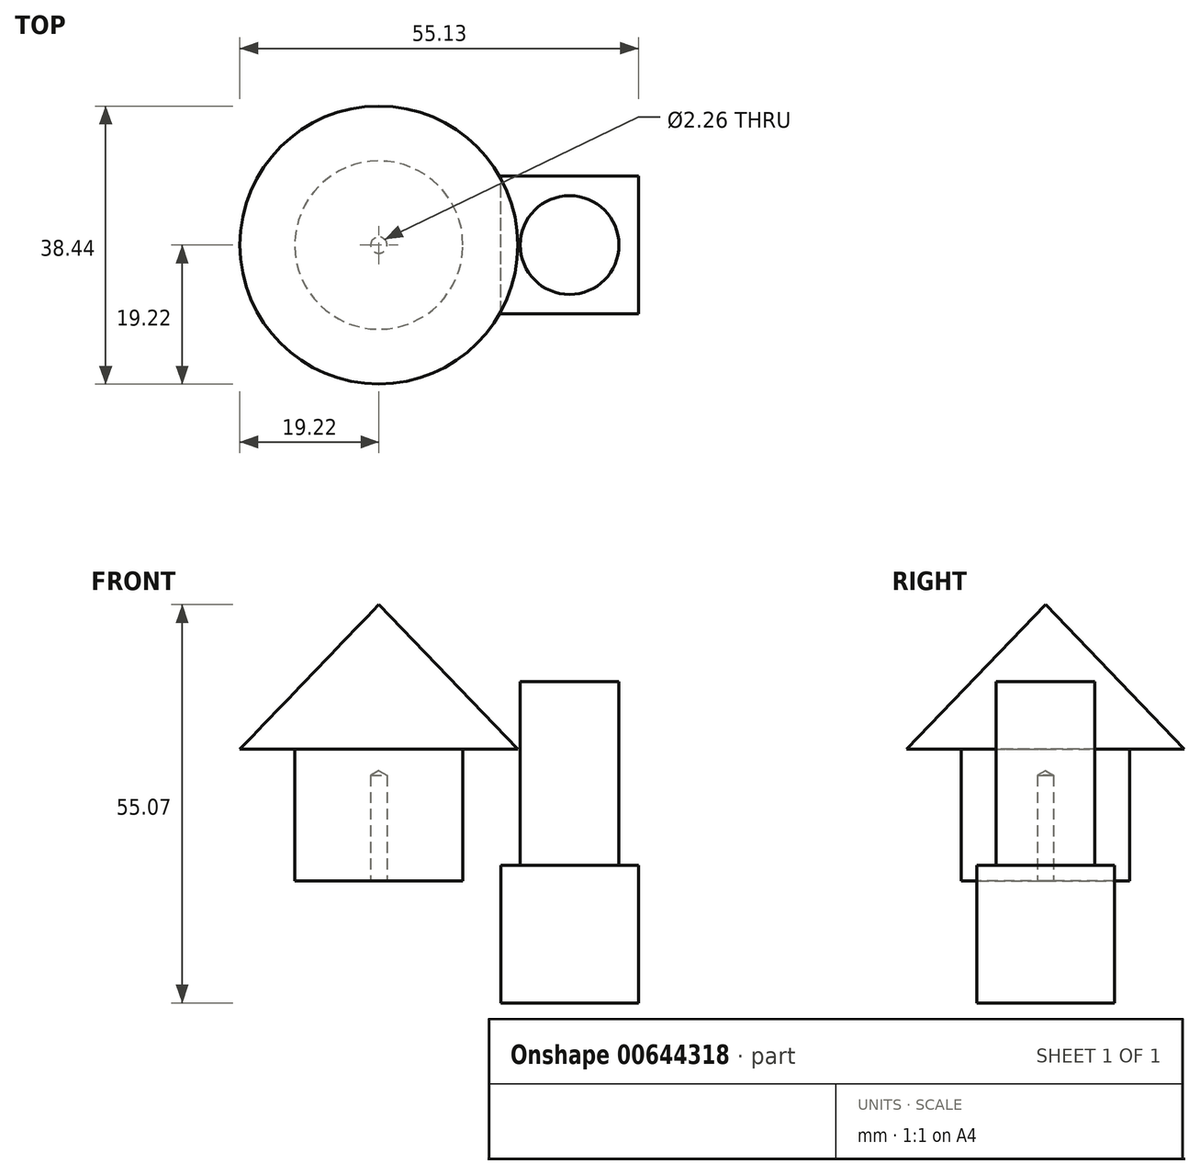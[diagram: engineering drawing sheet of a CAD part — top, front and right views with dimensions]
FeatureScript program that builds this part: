
annotation { "Feature Type Name" : "Feature", "Feature Type Description" : "" }
export const myFeature = defineFeature(function(context is Context, id is Id, definition is map)
    precondition{}
    {
        {
            var Q0;
            Q0=qCreatedBy(makeId("Top.planeOp"),FACE);
            var sketch = newSketch(context, id + "F0", { "sketchPlane" : qUnion([Q0])});
            skLineSegment(sketch, "E0.bottom", {"start": v(-9.53, -9.53) * mm, "end": v(9.53, -9.53) * mm});
            skLineSegment(sketch, "E0.top", {"start": v(-9.53, 9.53) * mm, "end": v(9.52, 9.53) * mm});
            skLineSegment(sketch, "E0.left", {"start": v(-9.53, -9.52) * mm, "end": v(-9.53, 9.53) * mm});
            skLineSegment(sketch, "E0.right", {"start": v(9.52, -9.52) * mm, "end": v(9.52, 9.53) * mm});
            skPoint(sketch, "E0.middle", {"position": v(0, 0) * mm});
            skSolve(sketch);
        }
        {
            var Q0;
            Q0 = qSketchRegion(id + "F0", true);
            extrude(context, id + "F1", {"entities" : qUnion([Q0]), "endBound" : BoundingType.SYMMETRIC, "depth" : 19.05 * mm, "offsetDistance" : 25.4 * mm});
        }
        {
            var Q0;
            Q0=makeQuery(id+"F1.opExtrude","CAP_FACE",FACE,{"disambiguationData":[OSD([sQuery(id+"F0.wireOp",EDGE,"E0.bottom"),sQuery(id+"F0.wireOp",EDGE,"E0.top"),sQuery(id+"F0.wireOp",EDGE,"E0.left"),sQuery(id+"F0.wireOp",EDGE,"E0.right")])],"isStart":false});
            var sketch = newSketch(context, id + "F2", { "sketchPlane" : qUnion([Q0])});
            skCircle(sketch, "E1", {"center": v(0, 0) * mm, "radius": 6.83 * mm});
            skSolve(sketch);
        }
        {
            var Q0;
            Q0 = qSketchRegion(id + "F2", true);
            extrude(context, id + "F3", {"entities" : qUnion([Q0]), "operationType" : NewBodyOperationType.ADD, "depth" : 25.4 * mm, "offsetDistance" : 25.4 * mm});
        }
        {
            var Q0;
            Q0=qCreatedBy(makeId("Front.planeOp"),FACE);
            var sketch = newSketch(context, id + "F4", { "sketchPlane" : qUnion([Q0])});
            skLineSegment(sketch, "E2", {"start": v(-26.38, 45.54) * mm, "end": v(-45.6, 25.56) * mm});
            skLineSegment(sketch, "E3", {"start": v(-45.6, 25.56) * mm, "end": v(-38.02, 25.56) * mm});
            skLineSegment(sketch, "E4", {"start": v(-38.02, 25.56) * mm, "end": v(-38.02, 7.32) * mm});
            skLineSegment(sketch, "E5", {"start": v(-38.02, 7.32) * mm, "end": v(-26.38, 7.32) * mm});
            skLineSegment(sketch, "E6", {"start": v(-26.38, 7.32) * mm, "end": v(-26.38, 45.54) * mm});
            skSolve(sketch);
        }
        {
            var Q0;
            Q0 = qSketchRegion(id + "F4", true);
            var Q1;
            Q1=sQuery(id+"F4.wireOp",EDGE,"E6");
            revolve(context, id + "F5", {"entities" : qUnion([Q0]), "axis" : qUnion([Q1]), "revolveType" : RevolveType.FULL});
        }
        {
            var Q0;
            Q0=makeQuery(id+"F5.opRevolve","SWEPT_FACE",FACE,{"disambiguationData":[OSD([sQuery(id+"F4.wireOp",EDGE,"E5")])]});
            var sketch = newSketch(context, id + "F6", { "sketchPlane" : qUnion([Q0])});
            skPoint(sketch, "E7", {"position": v(-26.38, 0) * mm});
            skSolve(sketch);
        }
        {
            var Q0;
            Q0=sQuery(id+"F6.wireOp",VERTEX,"E7");
            var Q1;
            Q1=makeQuery(id+"F5.opRevolve","SWEPT_BODY",BODY,{"disambiguationData":[OSD([sQuery(id+"F4.wireOp",EDGE,"E2"),sQuery(id+"F4.wireOp",EDGE,"E3"),sQuery(id+"F4.wireOp",EDGE,"E4"),sQuery(id+"F4.wireOp",EDGE,"E5"),sQuery(id+"F4.wireOp",EDGE,"E6")])]});
            hole(context, id + "F7", {"style" : HoleStyle.SIMPLE, "endStyle" : HoleEndStyle.BLIND, "standardTappedOrClearance" : lookupTablePath({ "standard" : "ANSI", "engagement" : "75%", "pitch" : "40 tpi", "size" : "#4", "type" : "Tapped" }), "standardBlindInLast" : lookupTablePath({ "standard" : "ANSI", "engagement" : "75%", "pitch" : "40 tpi", "size" : "#4", "type" : "Tapped" }), "holeDiameter" : 2.26 * mm, "majorDiameter" : 2.84 * mm, "showTappedDepth" : true, "holeDepth" : 14.6 * mm, "tappedDepth" : 12.7 * mm, "tapClearance" : 3, "locations" : qUnion([Q0]), "scope" : qUnion([Q1])});
        }
    });
